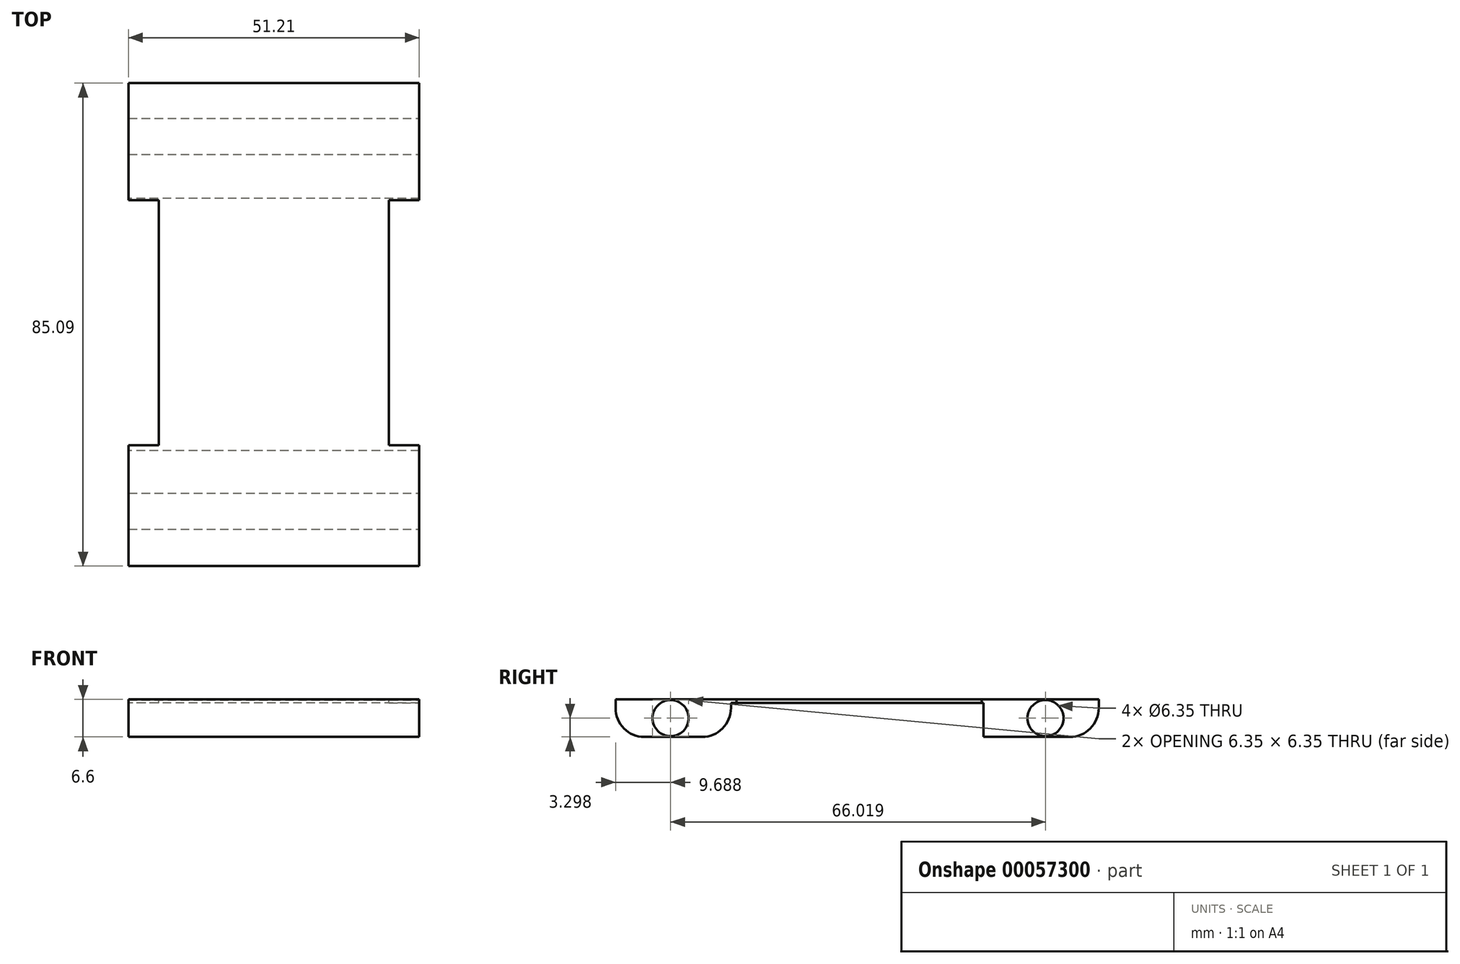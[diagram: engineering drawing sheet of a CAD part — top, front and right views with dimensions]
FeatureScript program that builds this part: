
annotation { "Feature Type Name" : "Feature", "Feature Type Description" : "" }
export const myFeature = defineFeature(function(context is Context, id is Id, definition is map)
    precondition{}
    {
        {
            var Q0;
            Q0=qCreatedBy(makeId("Top.planeOp"),FACE);
            var sketch = newSketch(context, id + "F0", { "sketchPlane" : qUnion([Q0])});
            skLineSegment(sketch, "E0.bottom", {"start": v(-30.33, 27.52) * mm, "end": v(20.88, 27.52) * mm});
            skLineSegment(sketch, "E0.top", {"start": v(-30.33, -57.57) * mm, "end": v(20.88, -57.57) * mm});
            skLineSegment(sketch, "E0.left", {"start": v(-30.33, 27.52) * mm, "end": v(-30.33, -57.57) * mm});
            skLineSegment(sketch, "E0.right", {"start": v(20.88, 27.52) * mm, "end": v(20.88, -57.57) * mm});
            skSolve(sketch);
        }
        {
            var Q0;
            Q0 = qSketchRegion(id + "F0", true);
            extrude(context, id + "F1", {"entities" : qUnion([Q0]), "oppositeDirection" : true, "depth" : 6.6 * mm});
        }
        {
            var Q0;
            Q0=makeQuery(id+"F1.opExtrude","SWEPT_FACE",FACE,{"disambiguationData":[OSD([sQuery(id+"F0.wireOp",EDGE,"E0.right")])]});
            var sketch = newSketch(context, id + "F2", { "sketchPlane" : qUnion([Q0])});
            skLineSegment(sketch, "E1", {"start": v(-57.57, -3.3) * mm, "end": v(27.52, -3.3) * mm, "construction": true});
            skCircle(sketch, "E2", {"center": v(18.14, -3.3) * mm, "radius": 3.18 * mm});
            skCircle(sketch, "E3", {"center": v(-47.88, -3.3) * mm, "radius": 3.18 * mm});
            skSolve(sketch);
        }
        {
            var Q0;
            Q0=makeQuery(id+"F2.imprint","IMPRINT",FACE,{"disambiguationData":[TD([[makeQuery(id+"F2.imprint","IMPRINT",EDGE,{"derivedFrom":sQuery(id+"F2.wireOp",EDGE,"E2")}),1.0]])]});
            var Q1;
            Q1=makeQuery(id+"F2.imprint","IMPRINT",FACE,{"disambiguationData":[TD([[makeQuery(id+"F2.imprint","IMPRINT",EDGE,{"derivedFrom":sQuery(id+"F2.wireOp",EDGE,"E3")}),1.0]])]});
            extrude(context, id + "F3", {"entities" : qUnion([Q0, Q1]), "operationType" : NewBodyOperationType.REMOVE, "oppositeDirection" : true, "depth" : 95.22 * mm});
        }
        {
            var Q0;
            Q0=makeQuery(id+"F1.opExtrude","CAP_FACE",FACE,{"disambiguationData":[OSD([sQuery(id+"F0.wireOp",EDGE,"E0.bottom"),sQuery(id+"F0.wireOp",EDGE,"E0.top"),sQuery(id+"F0.wireOp",EDGE,"E0.left"),sQuery(id+"F0.wireOp",EDGE,"E0.right")])],"isStart":false});
            var sketch = newSketch(context, id + "F4", { "sketchPlane" : qUnion([Q0])});
            skLineSegment(sketch, "E4", {"start": v(20.88, 37.25) * mm, "end": v(-30.33, 37.25) * mm});
            skLineSegment(sketch, "E5", {"start": v(20.88, -7.2) * mm, "end": v(-30.33, -7.2) * mm});
            skSolve(sketch);
        }
        {
            var Q0;
            Q0 = qSketchRegion(id + "F4", true);
            var Q1;
            {var subQ0=sQuery(id+"F4.wireOp",EDGE,"E4");Q1=makeQuery(id+"F4.imprint","IMPRINT",FACE,{"disambiguationData":[TD([[makeQuery(id+"F4.imprint","IMPRINT",EDGE,{"derivedFrom":subQ0}),1.0]])]});}
            extrude(context, id + "F5", {"entities" : qUnion([Q0, Q1]), "operationType" : NewBodyOperationType.REMOVE, "oppositeDirection" : true, "depth" : 5.96 * mm});
        }
        {
            var Q0;
            Q0=makeQuery(id+"F5.boolean.opBoolean","COPY",EDGE,{"derivedFrom":makeQuery(id+"F5.opExtrude","CAP_EDGE",EDGE,{"disambiguationData":[OSD([sQuery(id+"F4.wireOp",EDGE,"E4")])],"isStart":true})});
            var Q1;
            Q1=makeQuery(id+"F1.opExtrude","CAP_EDGE",EDGE,{"disambiguationData":[OSD([sQuery(id+"F0.wireOp",EDGE,"E0.top")])],"isStart":false});
            var Q2;
            Q2=makeQuery(id+"F5.boolean.opBoolean","COPY",EDGE,{"derivedFrom":makeQuery(id+"F5.opExtrude","CAP_EDGE",EDGE,{"disambiguationData":[OSD([sQuery(id+"F4.wireOp",EDGE,"E5")])],"isStart":true})});
            var Q3;
            Q3=makeQuery(id+"F1.opExtrude","CAP_EDGE",EDGE,{"disambiguationData":[OSD([sQuery(id+"F0.wireOp",EDGE,"E0.bottom")])],"isStart":false});
            fillet(context, id + "F6", {"entities" : qUnion([Q0, Q1, Q2, Q3]), "radius" : 5.08 * mm, "tangentPropagation" : true, "allowEdgeOverflow" : false});
        }
        {
            var Q0;
            Q0=makeQuery(id+"F1.opExtrude","CAP_FACE",FACE,{"disambiguationData":[OSD([sQuery(id+"F0.wireOp",EDGE,"E0.bottom"),sQuery(id+"F0.wireOp",EDGE,"E0.top"),sQuery(id+"F0.wireOp",EDGE,"E0.left"),sQuery(id+"F0.wireOp",EDGE,"E0.right")])],"isStart":true});
            var sketch = newSketch(context, id + "F7", { "sketchPlane" : qUnion([Q0])});
            skLineSegment(sketch, "E6", {"start": v(20.88, 6.9) * mm, "end": v(15.54, 6.9) * mm});
            skLineSegment(sketch, "E7", {"start": v(15.54, 6.9) * mm, "end": v(15.54, -36.28) * mm});
            skLineSegment(sketch, "E8", {"start": v(15.54, -36.28) * mm, "end": v(20.88, -36.28) * mm});
            skLineSegment(sketch, "E9", {"start": v(-30.33, -36.28) * mm, "end": v(-25, -36.28) * mm});
            skLineSegment(sketch, "E10", {"start": v(-25, -36.28) * mm, "end": v(-25, 6.9) * mm});
            skLineSegment(sketch, "E11", {"start": v(-25, 6.9) * mm, "end": v(-30.33, 6.9) * mm});
            skSolve(sketch);
        }
        {
            var Q0;
            {var subQ0=sQuery(id+"F7.wireOp",EDGE,"E9");Q0=makeQuery(id+"F7.imprint","IMPRINT",FACE,{"disambiguationData":[TD([[makeQuery(id+"F7.imprint","IMPRINT",EDGE,{"derivedFrom":subQ0}),1.0]])]});}
            var Q1;
            {var subQ0=sQuery(id+"F7.wireOp",EDGE,"E6");Q1=makeQuery(id+"F7.imprint","IMPRINT",FACE,{"disambiguationData":[TD([[makeQuery(id+"F7.imprint","IMPRINT",EDGE,{"derivedFrom":subQ0}),1.0]])]});}
            extrude(context, id + "F8", {"entities" : qUnion([Q0, Q1]), "operationType" : NewBodyOperationType.REMOVE, "oppositeDirection" : true, "depth" : 25.4 * mm});
        }
    });
